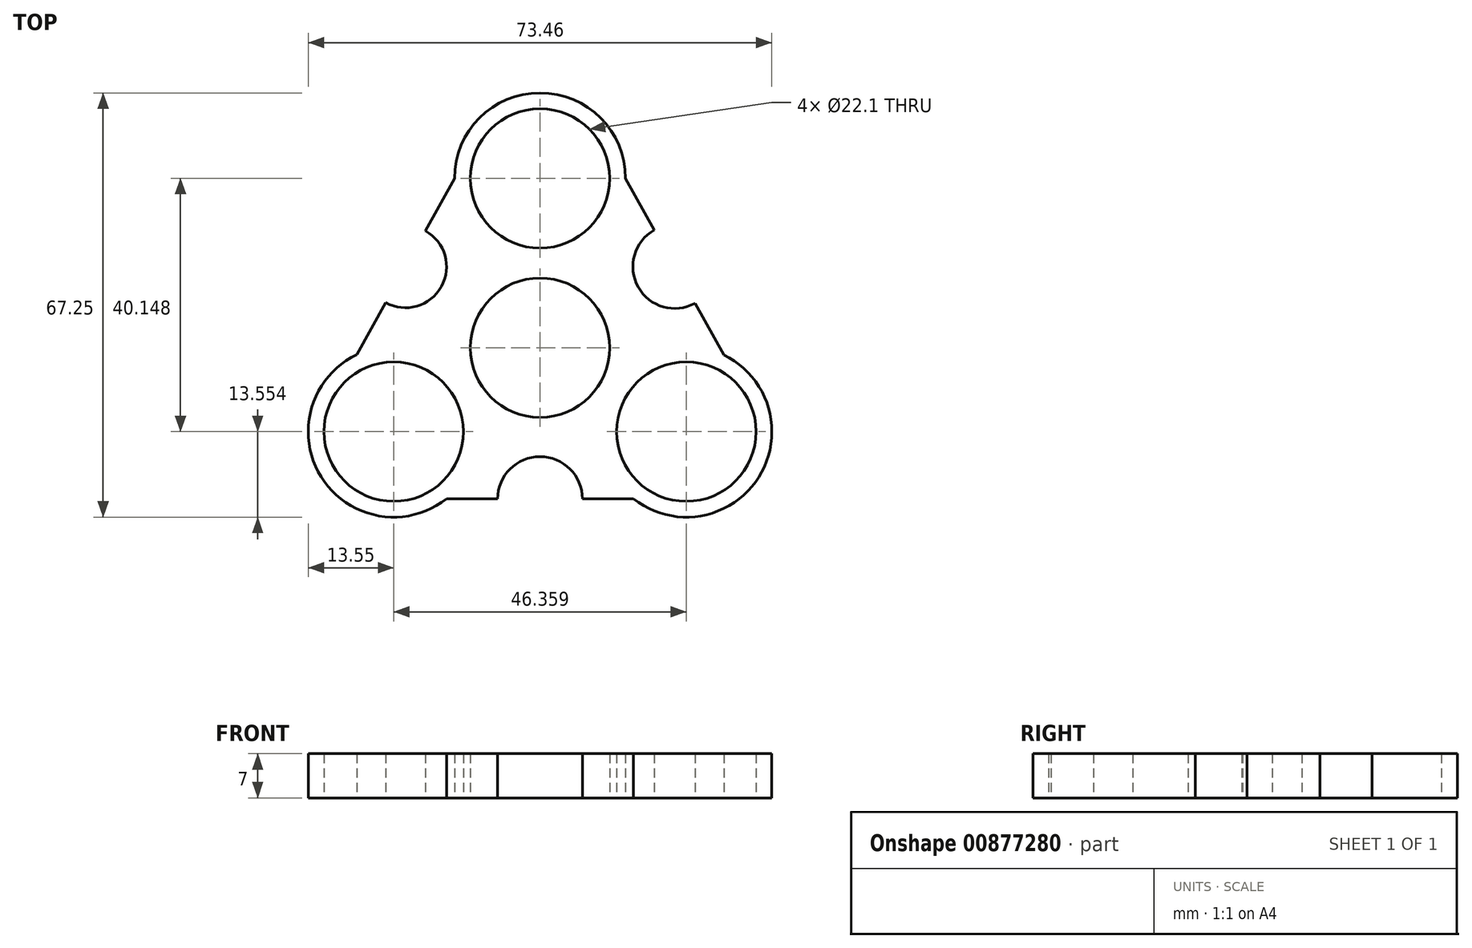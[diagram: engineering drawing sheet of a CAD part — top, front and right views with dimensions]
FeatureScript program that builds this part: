
annotation { "Feature Type Name" : "Feature", "Feature Type Description" : "" }
export const myFeature = defineFeature(function(context is Context, id is Id, definition is map)
    precondition{}
    {
        {
            var Q0;
            Q0=qCreatedBy(makeId("Top.planeOp"),FACE);
            var sketch = newSketch(context, id + "F0", { "sketchPlane" : qUnion([Q0])});
            skCircle(sketch, "E0", {"center": v(0, 0) * mm, "radius": 11.05 * mm});
            skArc(sketch, "E1", {"start": v(13.55, 26.84) * mm, "mid": v(0, 40.4) * mm, "end": v(-13.55, 26.84) * mm});
            skCircle(sketch, "E2", {"center": v(0, 26.84) * mm, "radius": 11.05 * mm});
            skCircle(sketch, "E3.1.0", {"center": v(-23.18, -13.3) * mm, "radius": 11.05 * mm});
            skArc(sketch, "E3.1.1", {"start": v(-29.04, -1.09) * mm, "mid": v(-34.69, -20.46) * mm, "end": v(-14.82, -23.97) * mm});
            skCircle(sketch, "E3.2.0", {"center": v(23.18, -13.3) * mm, "radius": 11.05 * mm});
            skArc(sketch, "E3.2.1", {"start": v(14.82, -23.97) * mm, "mid": v(34.66, -20.5) * mm, "end": v(29.14, -1.13) * mm});
            skPoint(sketch, "E3.center", {"position": v(0, 0.08) * mm});
            skLineSegment(sketch, "E4", {"start": v(14.82, -23.97) * mm, "end": v(6.71, -23.97) * mm});
            skLineSegment(sketch, "E5", {"start": v(-13.55, 26.84) * mm, "end": v(-18.16, 18.52) * mm});
            skLineSegment(sketch, "E6", {"start": v(13.55, 26.84) * mm, "end": v(18.11, 18.65) * mm});
            skArc(sketch, "E7", {"start": v(-24.47, 7.16) * mm, "mid": v(-15.63, 9.7) * mm, "end": v(-18.16, 18.52) * mm});
            skArc(sketch, "E8", {"start": v(18.11, 18.65) * mm, "mid": v(15.55, 9.63) * mm, "end": v(24.57, 7.06) * mm});
            skArc(sketch, "E9", {"start": v(6.71, -23.97) * mm, "mid": v(0, -17.26) * mm, "end": v(-6.71, -23.97) * mm});
            skLineSegment(sketch, "E10.trimOffspring", {"start": v(24.57, 7.06) * mm, "end": v(29.14, -1.13) * mm});
            skLineSegment(sketch, "E11.trimOffspring", {"start": v(-6.71, -23.97) * mm, "end": v(-14.82, -23.97) * mm});
            skLineSegment(sketch, "E12.trimOffspring", {"start": v(-24.47, 7.16) * mm, "end": v(-29.04, -1.09) * mm});
            skSolve(sketch);
        }
        {
            var Q0;
            Q0 = qSketchRegion(id + "F0", true);
            extrude(context, id + "F1", {"entities" : qUnion([Q0]), "depth" : 7 * mm, "offsetDistance" : 25 * mm});
        }
    });
